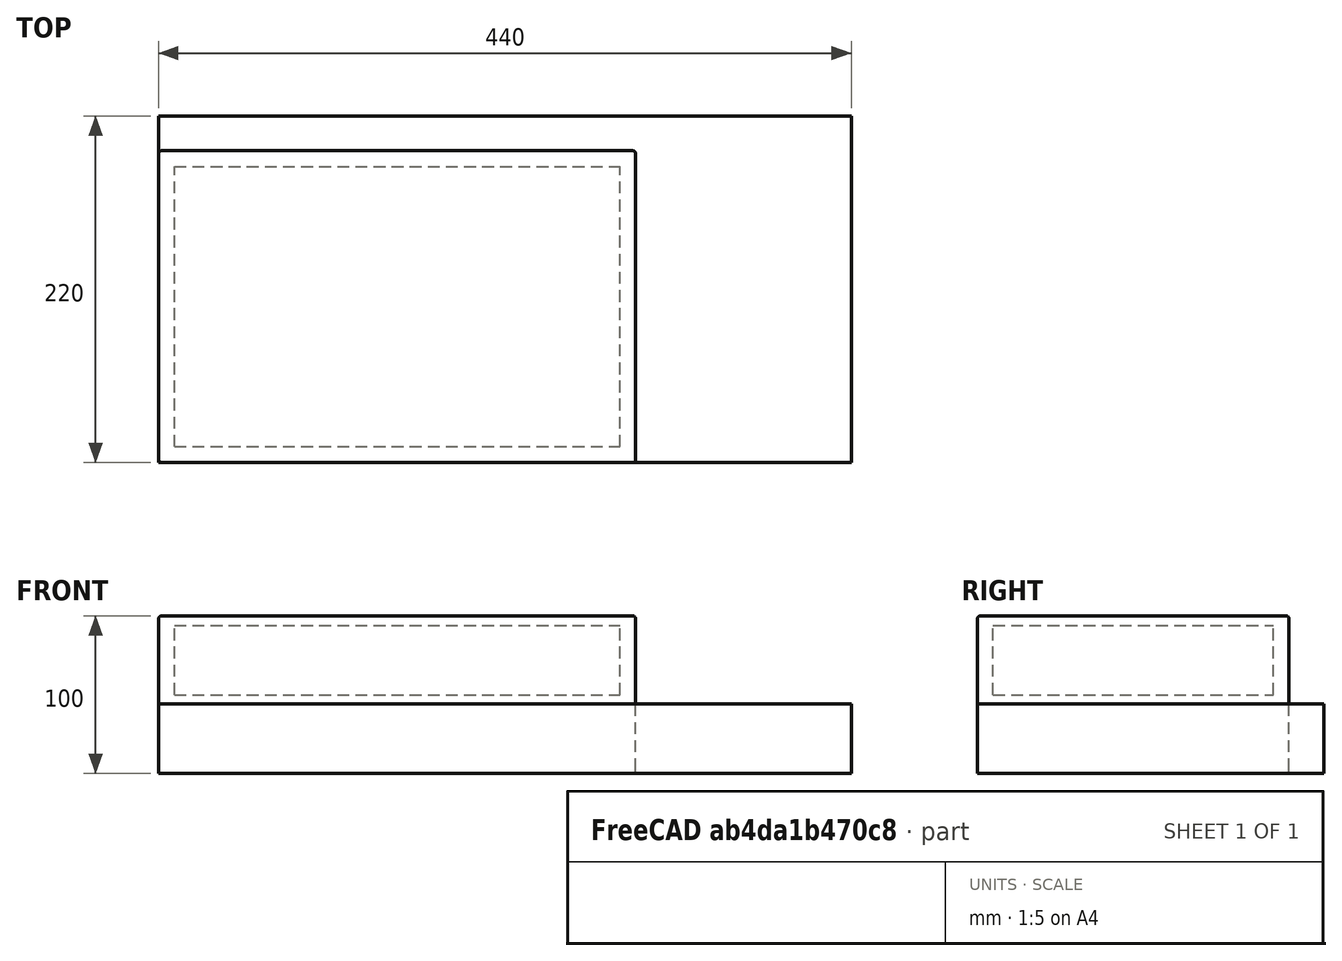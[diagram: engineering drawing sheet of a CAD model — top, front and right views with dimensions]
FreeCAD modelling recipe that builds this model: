
FCSTD DOCUMENT  (FreeCAD 0.16R6706 (Git))
Label: 1
License: All rights reserved
LicenseURL: http://en.wikipedia.org/wiki/All_rights_reserved
objects: Part::Box×4, Part::Part2DObjectPython×2, Part::Fillet×1
note: 7 computed .brp shape members not serialized (recipe doc carries the construction recipe); baked Part::Feature solids carry a one-line shape summary decoded from their .brp

FEATURE [Part::Box] Box  label="48switcher"
  Height = 44
  Length = 440
  Width = 220
FEATURE [Part::Box] Box001  label="24swicher1"
  Height = 44
  Length = 283
  Placement = pos=(10,10,50) rot=(0,0,1;0rad)
  Width = 178
FEATURE [Part::Box] Box003  label="24swicher2"
  Height = 44
  Length = 283
  Placement = pos=(10,10,0) rot=(0,0,1;0rad)
  Width = 178
FEATURE [Part::Box] Box002  label=" 机箱"
  Height = 100
  Length = 303
  Width = 198
FEATURE [Part::Fillet] Fillet
  Base = -> Box002
  Edges = 12 edges r=2: [Edge1,Edge2,Edge3,Edge4,Edge5,Edge6,Edge7,Edge8,Edge9,Edge10,Edge11,Edge12]
FEATURE [Part::Part2DObjectPython] Shape2DView  # Draft 2D object (typed FeaturePython)
  Base = -> Box003
  FaceNumbers = [2]
  HiddenLines = false
  Projection = (0,0,1)
  ProjectionMode = 0
  SegmentLength = 0.05
  Tessellation = false
FEATURE [Part::Part2DObjectPython] Shape2DView001  # Draft 2D object (typed FeaturePython)
  Base = -> Box003
  FaceNumbers = [5]
  HiddenLines = false
  Projection = (0,-1,5.9605e-08)
  ProjectionMode = 0
  SegmentLength = 0.05
  Tessellation = false
